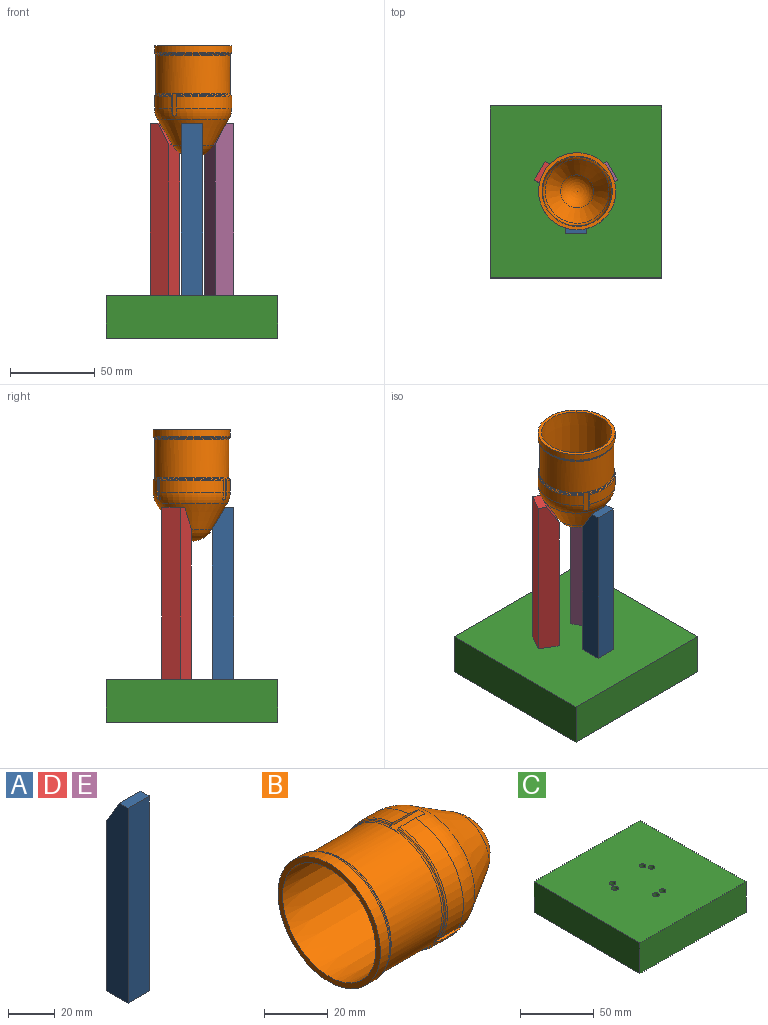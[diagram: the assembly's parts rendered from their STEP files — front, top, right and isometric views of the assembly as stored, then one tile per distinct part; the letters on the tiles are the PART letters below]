
ASSEMBLY  parts=5 mates=10
PART A: 11 faces, bbox 12.7x12.7x101.6 mm
  f0: plane 12.7x12.7mm, normal (0,0,-1), area 142.5mm2, adj f1,f4,f5,f6,f8,f10
  f1: plane 88.9x12.7mm, normal (0,1,0), area 1129mm2, adj f0,f2,f5,f6
  f2: plane 12.7x12.7mm, normal (0,0.86,0.51), area 187.4mm2, adj f1,f3,f5,f6
  f3: plane 12.7x5.19mm, normal (0,0,1), area 65.9mm2, adj f2,f4,f5,f6
  f4: plane 101.6x12.7mm, normal (0,-1,0), area 1290.3mm2, adj f0,f3,f5,f6
  f5: plane 101.6x12.7mm, normal (1,0,0), area 1242.6mm2, adj f0,f1,f2,f3,f4
  f6: plane 101.6x12.7mm, normal (-1,0,0), area 1242.6mm2, adj f0,f1,f2,f3,f4
  f7: cone r=0mm half-angle=59deg, axis (0,0,-1), area 10.9mm2, adj f8
  f8: cylinder r=1.73mm len=15.08mm, axis (0,0,-1), area 163.7mm2, adj f0,f7
  f9: cone r=0mm half-angle=59deg, axis (0,0,-1), area 10.9mm2, adj f10
  f10: cylinder r=1.73mm len=15.08mm, axis (0,0,-1), area 163.7mm2, adj f0,f9
PART B: 34 faces, bbox 66x49.5x49.4 mm
  f0: torus R=22.84mm, axis (1,0,0), area 30.6mm2, adj f1,f13,f26,f27,f31,f32
  f1: cone r=22.52mm half-angle=45deg, axis (1,0,0), area 19.4mm2, adj f0,f2,f27,f31
  f2: torus R=21.89mm, axis (1,0,0), area 31mm2, adj f1,f3,f27,f31
  f3: cylinder r=22.78mm len=32.71mm, axis (1,0,0), area 313.9mm2, adj f2,f18,f27,f31
  f4: torus R=22.84mm, axis (1,0,0), area 30.6mm2, adj f5,f13,f28,f29,f32,f33
  f5: cone r=22.52mm half-angle=45deg, axis (1,0,0), area 19.4mm2, adj f4,f6,f28,f33
  f6: torus R=21.89mm, axis (1,0,0), area 31mm2, adj f5,f7,f28,f33
  f7: cylinder r=22.78mm len=37.78mm, axis (1,0,0), area 313.9mm2, adj f6,f18,f28,f33
  f8: plane 45.54x45.54mm, normal (-1,0,0), area 276mm2, adj f9,f24
  f9: cylinder r=22.77mm len=45.54mm, axis (1,0,0), area 579.5mm2, adj f8,f10
  f10: torus R=21.88mm, axis (1,0,0), area 99.7mm2, adj f9,f11
  f11: cone r=22.21mm half-angle=45deg, axis (-1,0,0), area 60.3mm2, adj f10,f12
  f12: torus R=22.84mm, axis (1,0,0), area 96.9mm2, adj f11,f13
  f13: cylinder r=21.95mm len=43.89mm, axis (1,0,0), area 3122.5mm2, adj f0,f4,f12,f14
  f14: torus R=22.84mm, axis (1,0,0), area 30.6mm2, adj f13,f15,f25,f26,f29,f30
  f15: cone r=22.52mm half-angle=45deg, axis (1,0,0), area 19.4mm2, adj f14,f16,f25,f30
  f16: torus R=21.89mm, axis (1,0,0), area 31mm2, adj f15,f17,f25,f30
  f17: cylinder r=22.78mm len=32.71mm, axis (1,0,0), area 313.9mm2, adj f16,f18,f25,f30
  f18: torus R=9.19mm, axis (1,0,0), area 964.4mm2, adj f3,f7,f17,f19,f25,f26,f27,f28
  f19: cone r=11.78mm half-angle=30.6deg, axis (-1,0,0), area 1836mm2, adj f18,f20
  f20: sphere r=13.69mm, area 578.2mm2, adj f19
  f21: sphere r=11.33mm, area 395.9mm2, adj f22
  f22: cone r=18.86mm half-angle=30.6deg, axis (-1,0,0), area 1607.5mm2, adj f21,f23
  f23: torus R=9.19mm, axis (1,0,0), area 736.4mm2, adj f22,f24
  f24: cone r=20.75mm half-angle=0.5deg, axis (-1,0,0), area 4783.7mm2, adj f8,f23
  f25: plane 12.88x0.82mm, normal (0,1,0), area 8.5mm2, adj f14,f15,f16,f17,f18,f26
  f26: plane 13.32x3.18mm, normal (0,0,1), area 41.6mm2, adj f0,f14,f18,f25,f27
  f27: plane 12.88x0.82mm, normal (0,-1,0), area 8.5mm2, adj f0,f1,f2,f3,f18,f26
  f28: plane 12.88x0.72mm, normal (0,-0.5,0.87), area 8.5mm2, adj f4,f5,f6,f7,f18,f29
  f29: plane 13.32x2.75mm, normal (0,-0.87,-0.5), area 41.6mm2, adj f4,f14,f18,f28,f30
  f30: plane 12.88x0.72mm, normal (0,0.5,-0.87), area 8.5mm2, adj f14,f15,f16,f17,f18,f29
  f31: plane 12.88x0.72mm, normal (0,-0.5,-0.87), area 8.5mm2, adj f0,f1,f2,f3,f18,f32
  f32: plane 13.32x2.75mm, normal (0,0.87,-0.5), area 41.6mm2, adj f0,f4,f18,f31,f33
  f33: plane 12.88x0.72mm, normal (0,0.5,0.87), area 8.5mm2, adj f4,f5,f6,f7,f18,f32
PART C: 12 faces, bbox 101.6x101.6x25.4 mm
  f0: plane 101.6x25.4mm, normal (1,0,0), area 2580.6mm2, adj f1,f3,f4,f5
  f1: plane 101.6x25.4mm, normal (0,1,0), area 2580.6mm2, adj f0,f2,f4,f5
  f2: plane 101.6x25.4mm, normal (-1,0,0), area 2580.6mm2, adj f1,f3,f4,f5
  f3: plane 101.6x25.4mm, normal (0,-1,0), area 2580.6mm2, adj f0,f2,f4,f5
  f4: plane 101.6x101.6mm, normal (0,0,1), area 10227.3mm2, adj f0,f1,f2,f3,f6,f7,f8,f9
  f5: plane 101.6x101.6mm, normal (0,0,-1), area 10227.3mm2, adj f0,f1,f2,f3,f6,f7,f8,f9
  f6: cylinder r=2.25mm len=25.4mm, axis (0,0,1), area 358.7mm2, adj f4,f5
  f7: cylinder r=2.25mm len=25.4mm, axis (0,0,1), area 358.7mm2, adj f4,f5
  f8: cylinder r=2.25mm len=25.4mm, axis (0,0,1), area 358.7mm2, adj f4,f5
  f9: cylinder r=2.25mm len=25.4mm, axis (0,0,1), area 358.7mm2, adj f4,f5
  f10: cylinder r=2.25mm len=25.4mm, axis (0,0,1), area 358.7mm2, adj f4,f5
  f11: cylinder r=2.25mm len=25.4mm, axis (0,0,1), area 358.7mm2, adj f4,f5
PART D: same geometry as A
PART E: same geometry as A
PLACE A rot(axis=(-0.03,0,1),0deg) t=(178.76,36.94,-4.55)mm
PLACE B rot(axis=(0,1,0),90deg) t=(185.78,52.9,98.53)mm
PLACE C t=(185.11,52.73,-74.4)mm
PLACE D rot(axis=(0,0,-1),120deg) t=(174.61,66.13,-4.55)mm
PLACE E rot(axis=(0,0,1),120deg) t=(201.96,55.13,-4.55)mm
MATE cylindrical D.f7 <-> C.f9  axis (0,0,-1) through (170.77,64.68,-49)mm
MATE cylindrical A.f7 <-> C.f6  axis (0,0,-1) through (181.93,34.35,-49)mm
MATE cylindrical E.f9 <-> C.f10  axis (0,0,-1) through (199.44,64.68,-49)mm
MATE planar D.f0 <-> C.f4  axis (0,0,-1) through (177.86,64.25,-49)mm
MATE cylindrical A.f9 <-> C.f7  axis (0,0,-1) through (188.28,34.35,-49)mm
MATE cylindrical D.f9 <-> C.f8  axis (0,0,-1) through (167.6,59.18,-41.45)mm
MATE planar E.f0 <-> C.f4  axis (0,0,-1) through (201.03,61.93,-49)mm
MATE planar A.f0 <-> C.f4  axis (0,0,-1) through (185.11,34.35,-49)mm
MATE parallel B.f0 <-> C.f4  axis (0,0,1) through (185.78,52.9,98.53)mm
MATE cylindrical E.f7 <-> C.f11  axis (0,0,-1) through (202.62,59.18,-49)mm
